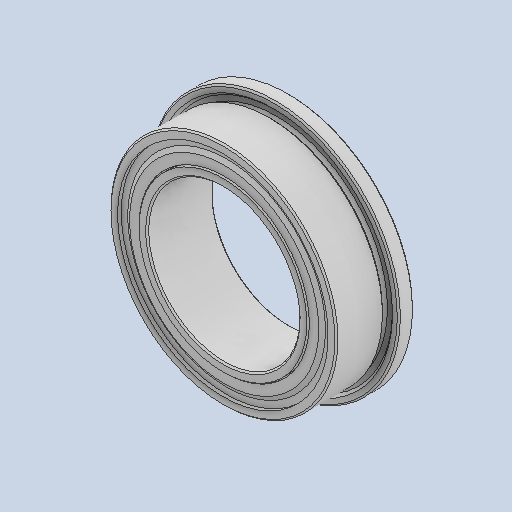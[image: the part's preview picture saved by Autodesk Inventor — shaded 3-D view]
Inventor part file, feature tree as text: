
AUTODESK INVENTOR PART (.ipt)
format: ipt  version: 2023 (Build 270158030, 158C)  size: 996,352 bytes
history: native  units: in
note: dims shown in document units (in); Inventor stores cm internally (conversion verified against a paired STEP export)
features: other x23, revolve x3
ambient origin geometry x8: Origin, YZ Plane, XZ Plane, XY Plane, X Axis, Y Axis, Z Axis, Center Point
bodies: Solid1 (feature_tree), Solid2 (feature_tree), Solid3 (feature_tree), Solid4 (feature_tree), Solid5 (feature_tree), Solid6 (feature_tree), Solid7 (feature_tree), Solid8 (feature_tree), Solid9 (feature_tree), Solid10 (feature_tree), Solid11 (feature_tree), Solid12 (feature_tree), Solid13 (feature_tree), Solid14 (feature_tree), Solid15 (feature_tree), Solid16 (feature_tree), Solid17 (feature_tree), Solid18 (feature_tree), Solid19 (feature_tree), Solid20 (feature_tree), Solid21 (feature_tree), Solid22 (feature_tree), Solid23 (feature_tree), Solid24 (feature_tree), Solid25 (feature_tree), Solid26 (feature_tree)
feature tree (26):
  revolve  "Revolve3"  [1 undecoded]
  other  "CirPattern3[1]"
  other  "CirPattern3[2]"
  other  "CirPattern3[3]"
  other  "CirPattern3[4]"
  other  "CirPattern3[5]"
  other  "CirPattern3[6]"
  other  "CirPattern3[7]"
  other  "CirPattern3[8]"
  other  "CirPattern3[9]"
  other  "CirPattern3[10]"
  other  "CirPattern3[11]"
  other  "Cut-Revolve1[1]"
  other  "Cut-Revolve1[2]"
  revolve  "Revolve4[1]"  [1 undecoded]
  revolve  "Revolve4[2]"  [1 undecoded]
  other  "CirPattern3[12]"
  other  "CirPattern3[13]"
  other  "CirPattern3[14]"
  other  "CirPattern3[15]"
  other  "CirPattern3[16]"
  other  "CirPattern3[17]"
  other  "CirPattern3[18]"
  other  "CirPattern3[19]"
  other  "CirPattern3[20]"
  other  "CirPattern3[21]"
note: 3 required parameter values undecoded (feature->parameter linkage not recoverable at this tier; creation-order binding heuristic only, values carry confidence <= 0.55)
